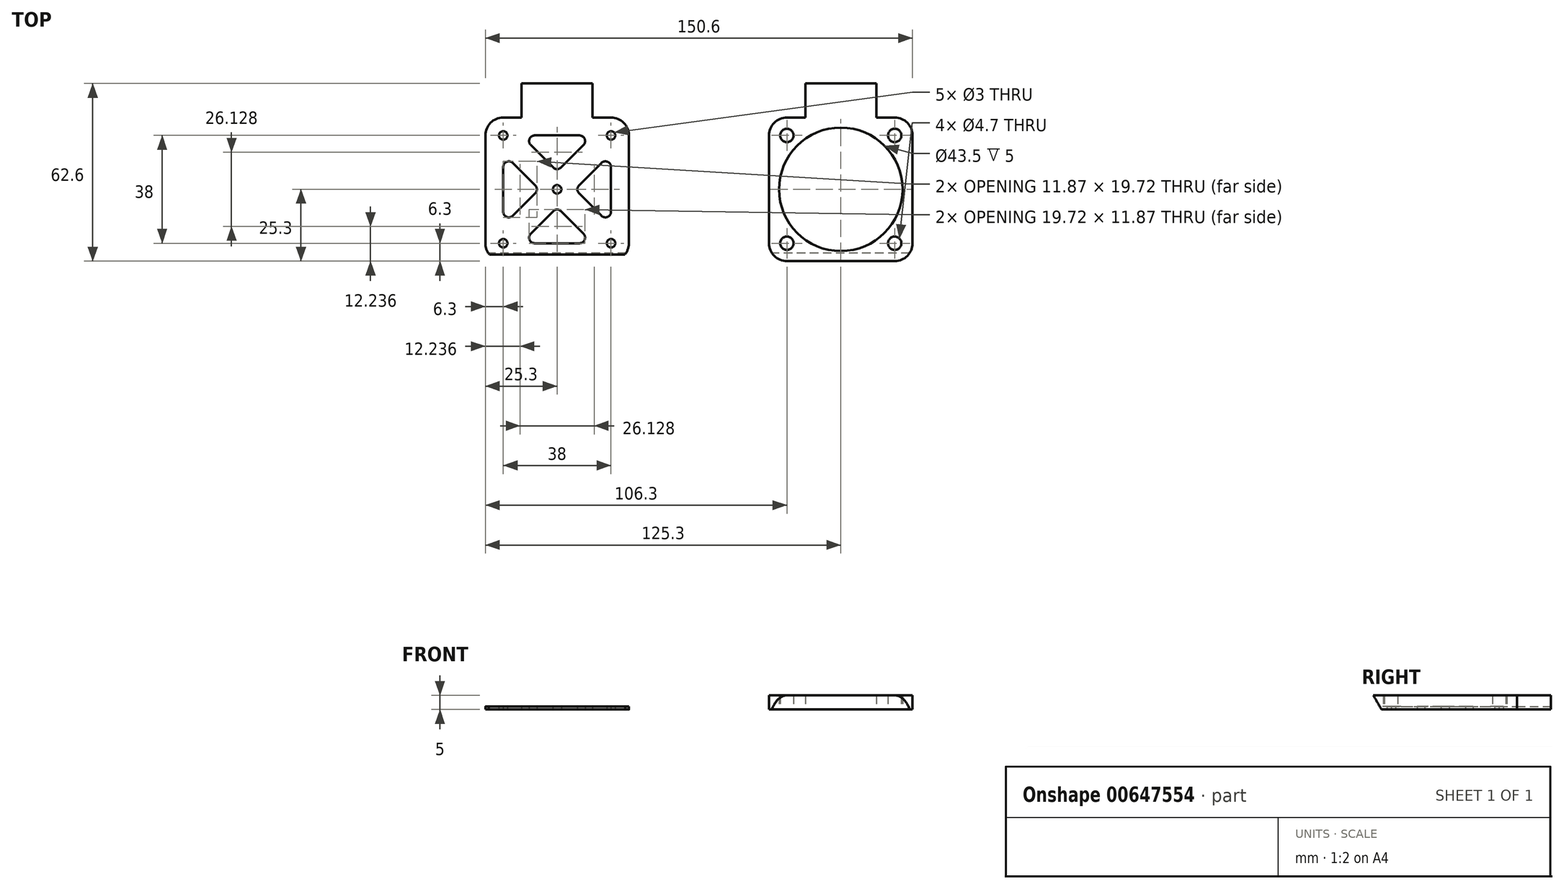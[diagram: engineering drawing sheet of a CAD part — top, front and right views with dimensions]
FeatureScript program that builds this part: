
annotation { "Feature Type Name" : "Feature", "Feature Type Description" : "" }
export const myFeature = defineFeature(function(context is Context, id is Id, definition is map)
    precondition{}
    {
        {
            var Q0;
            Q0=qCreatedBy(makeId("Top.planeOp"),FACE);
            var sketch = newSketch(context, id + "F0", { "sketchPlane" : qUnion([Q0])});
            skLineSegment(sketch, "E0.bottom", {"start": v(19, -25.3) * mm, "end": v(-19, -25.3) * mm});
            skLineSegment(sketch, "E0.top", {"start": v(19, 25.3) * mm, "end": v(-19, 25.3) * mm});
            skLineSegment(sketch, "E0.left", {"start": v(25.3, -19) * mm, "end": v(25.3, 19) * mm});
            skLineSegment(sketch, "E0.right", {"start": v(-25.3, -19) * mm, "end": v(-25.3, 19) * mm});
            skPoint(sketch, "E0.middle", {"position": v(0, 0) * mm});
            skLineSegment(sketch, "E1.bottom", {"start": v(-12.5, 25.3) * mm, "end": v(12.5, 25.3) * mm});
            skLineSegment(sketch, "E1.top", {"start": v(-12.5, 37.3) * mm, "end": v(12.5, 37.3) * mm});
            skLineSegment(sketch, "E1.left", {"start": v(-12.5, 25.3) * mm, "end": v(-12.5, 37.3) * mm});
            skLineSegment(sketch, "E1.right", {"start": v(12.5, 25.3) * mm, "end": v(12.5, 37.3) * mm});
            skPoint(sketch, "E2", {"position": v(0, 37.3) * mm});
            skCircle(sketch, "E3", {"center": v(0, 0) * mm, "radius": 21.75 * mm});
            skLineSegment(sketch, "E4.bottom", {"start": v(19, -19) * mm, "end": v(-19, -19) * mm, "construction": true});
            skLineSegment(sketch, "E4.top", {"start": v(19, 19) * mm, "end": v(-19, 19) * mm, "construction": true});
            skLineSegment(sketch, "E4.left", {"start": v(19, -19) * mm, "end": v(19, 19) * mm, "construction": true});
            skLineSegment(sketch, "E4.right", {"start": v(-19, -19) * mm, "end": v(-19, 19) * mm, "construction": true});
            skPoint(sketch, "E5.visualSharp", {"position": v(-25.3, 25.3) * mm});
            skArc(sketch, "E5.filletArc", {"start": v(-19, 25.3) * mm, "mid": v(-23.45, 23.45) * mm, "end": v(-25.3, 19) * mm});
            skPoint(sketch, "E6.visualSharp", {"position": v(25.3, 25.3) * mm});
            skArc(sketch, "E6.filletArc", {"start": v(25.3, 19) * mm, "mid": v(23.45, 23.45) * mm, "end": v(19, 25.3) * mm});
            skPoint(sketch, "E7.visualSharp", {"position": v(25.3, -25.3) * mm});
            skArc(sketch, "E7.filletArc", {"start": v(19, -25.3) * mm, "mid": v(23.45, -23.45) * mm, "end": v(25.3, -19) * mm});
            skPoint(sketch, "E8.visualSharp", {"position": v(-25.3, -25.3) * mm});
            skArc(sketch, "E8.filletArc", {"start": v(-25.3, -19) * mm, "mid": v(-23.45, -23.45) * mm, "end": v(-19, -25.3) * mm});
            skSolve(sketch);
        }
        {
            var Q0;
            Q0 = qSketchRegion(id + "F0", true);
            extrude(context, id + "F1", {"entities" : qUnion([Q0]), "depth" : 5 * mm, "offsetDistance" : 25 * mm});
        }
        {
            var Q0;
            Q0=sQuery(id+"F0.wireOp",VERTEX,"E4.bottom.end");
            var Q1;
            Q1=sQuery(id+"F0.wireOp",VERTEX,"E4.bottom.start");
            var Q2;
            Q2=sQuery(id+"F0.wireOp",VERTEX,"E4.top.end");
            var Q3;
            Q3=sQuery(id+"F0.wireOp",VERTEX,"E4.top.start");
            var Q4;
            Q4=makeQuery(id+"F1.opExtrude","SWEPT_BODY",BODY,{"disambiguationData":[OSD([sQuery(id+"F0.wireOp",EDGE,"E0.bottom"),sQuery(id+"F0.wireOp",EDGE,"E0.top"),sQuery(id+"F0.wireOp",EDGE,"E0.left"),sQuery(id+"F0.wireOp",EDGE,"E0.right"),sQuery(id+"F0.wireOp",EDGE,"E1.top"),sQuery(id+"F0.wireOp",EDGE,"E1.left"),sQuery(id+"F0.wireOp",EDGE,"E1.right"),sQuery(id+"F0.wireOp",EDGE,"E3"),sQuery(id+"F0.wireOp",EDGE,"E5.filletArc"),sQuery(id+"F0.wireOp",EDGE,"E6.filletArc"),sQuery(id+"F0.wireOp",EDGE,"E7.filletArc"),sQuery(id+"F0.wireOp",EDGE,"E8.filletArc")])]});
            hole(context, id + "F2", {"style" : HoleStyle.SIMPLE, "endStyle" : HoleEndStyle.THROUGH, "oppositeDirection" : true, "holeDiameter" : 4.7 * mm, "majorDiameter" : 5 * mm, "isTappedThrough" : true, "tappedDepth" : 12 * mm, "tapClearance" : 3, "startFromSketch" : true, "locations" : qUnion([Q0, Q1, Q2, Q3]), "scope" : qUnion([Q4])});
        }
        {
            var Q0;
            Q0=makeQuery(id+"F1.opExtrude","SWEPT_FACE",FACE,{"disambiguationData":[OSD([sQuery(id+"F0.wireOp",EDGE,"E0.right")])]});
            var sketch = newSketch(context, id + "F3", { "sketchPlane" : qUnion([Q0])});
            skLineSegment(sketch, "E9.0", {"start": v(19, 0) * mm, "end": v(25.3, 0) * mm});
            skLineSegment(sketch, "E10.0", {"start": v(25.3, 5) * mm, "end": v(25.3, 0) * mm});
            skLineSegment(sketch, "E11.0", {"start": v(19, 5) * mm, "end": v(25.3, 5) * mm, "construction": true});
            skLineSegment(sketch, "E12.0", {"start": v(19, 5) * mm, "end": v(19, 0) * mm, "construction": true});
            skLineSegment(sketch, "E13", {"start": v(22.41, 0) * mm, "end": v(25.3, 5) * mm});
            skPoint(sketch, "E14", {"position": v(25.3, 2.5) * mm});
            skLineSegment(sketch, "E15.0", {"start": v(-37.3, 5) * mm, "end": v(-37.3, 0) * mm, "construction": true});
            skSolve(sketch);
        }
        {
            var Q0;
            {var subQ0=sQuery(id+"F3.wireOp",EDGE,"E10.0");Q0=makeQuery(id+"F3.imprint","IMPRINT",FACE,{"disambiguationData":[TD([[makeQuery(id+"F3.imprint","IMPRINT",EDGE,{"derivedFrom":subQ0}),-1.0]])]});}
            var Q1;
            Q1=makeQuery(id+"F1.opExtrude","SWEPT_FACE",FACE,{"disambiguationData":[OSD([sQuery(id+"F0.wireOp",EDGE,"E0.left")])]});
            extrude(context, id + "F4", {"entities" : qUnion([Q0]), "operationType" : NewBodyOperationType.REMOVE, "endBound" : BoundingType.UP_TO_SURFACE, "oppositeDirection" : true, "depth" : 25 * mm, "endBoundEntityFace" : qUnion([Q1]), "offsetDistance" : 25 * mm});
        }
        {
            var Q0;
            Q0=qCreatedBy(makeId("Top.planeOp"),FACE);
            var sketch = newSketch(context, id + "F5", { "sketchPlane" : qUnion([Q0])});
            skLineSegment(sketch, "E16.0", {"start": v(-25.3, -19) * mm, "end": v(-25.3, 19) * mm});
            skPoint(sketch, "E17.0", {"position": v(-24.3, -22.41) * mm});
            skArc(sketch, "E18.0", {"start": v(-25.3, -19) * mm, "mid": v(-25.04, -20.78) * mm, "end": v(-24.3, -22.41) * mm});
            skLineSegment(sketch, "E19.0", {"start": v(24.3, -22.41) * mm, "end": v(-24.3, -22.41) * mm});
            skArc(sketch, "E20.0", {"start": v(24.3, -22.41) * mm, "mid": v(25.04, -20.78) * mm, "end": v(25.3, -19) * mm});
            skLineSegment(sketch, "E21.0", {"start": v(25.3, -19) * mm, "end": v(25.3, 19) * mm});
            skArc(sketch, "E22.0", {"start": v(25.3, 19) * mm, "mid": v(23.45, 23.45) * mm, "end": v(19, 25.3) * mm});
            skLineSegment(sketch, "E23.0", {"start": v(19, 25.3) * mm, "end": v(12.5, 25.3) * mm});
            skLineSegment(sketch, "E24.0", {"start": v(12.5, 25.3) * mm, "end": v(12.5, 37.3) * mm});
            skLineSegment(sketch, "E25.0", {"start": v(-12.5, 37.3) * mm, "end": v(12.5, 37.3) * mm});
            skLineSegment(sketch, "E26.0", {"start": v(-12.5, 25.3) * mm, "end": v(-12.5, 37.3) * mm});
            skLineSegment(sketch, "E27.0", {"start": v(-12.5, 25.3) * mm, "end": v(-19, 25.3) * mm});
            skArc(sketch, "E28.0", {"start": v(-19, 25.3) * mm, "mid": v(-23.45, 23.45) * mm, "end": v(-25.3, 19) * mm});
            skLineSegment(sketch, "E29.0.0", {"start": v(-25.3, 19) * mm, "end": v(-25.3, -19) * mm});
            skCircle(sketch, "E30", {"center": v(0, 0) * mm, "radius": 1.5 * mm});
            skCircle(sketch, "E31", {"center": v(-19, 19) * mm, "radius": 1.5 * mm});
            skCircle(sketch, "E32", {"center": v(-19, 19) * mm, "radius": 6.3 * mm});
            skCircle(sketch, "E33", {"center": v(19, 19) * mm, "radius": 1.5 * mm});
            skCircle(sketch, "E34", {"center": v(19, 19) * mm, "radius": 6.3 * mm});
            skArc(sketch, "E35", {"start": v(24.3, -22.41) * mm, "mid": v(19, -12.7) * mm, "end": v(13.7, -22.41) * mm});
            skArc(sketch, "E36", {"start": v(-13.7, -22.41) * mm, "mid": v(-19, -12.7) * mm, "end": v(-24.3, -22.41) * mm});
            skLineSegment(sketch, "E37", {"start": v(-19, 7.87) * mm, "end": v(-19, -7.87) * mm});
            skLineSegment(sketch, "E38", {"start": v(-7.87, -19) * mm, "end": v(7.87, -19) * mm});
            skLineSegment(sketch, "E39", {"start": v(19, -7.87) * mm, "end": v(19, 7.87) * mm});
            skLineSegment(sketch, "E40", {"start": v(7.87, 19) * mm, "end": v(-7.87, 19) * mm});
            skLineSegment(sketch, "E41", {"start": v(-9.29, 15.59) * mm, "end": v(-1.41, 7.71) * mm});
            skLineSegment(sketch, "E42", {"start": v(9.29, -15.59) * mm, "end": v(1.41, -7.71) * mm});
            skLineSegment(sketch, "E43", {"start": v(-15.59, -9.29) * mm, "end": v(-7.71, -1.41) * mm});
            skLineSegment(sketch, "E44", {"start": v(-9.29, -15.59) * mm, "end": v(-1.41, -7.71) * mm});
            skPoint(sketch, "E45.visualSharp", {"position": v(-19, 12.7) * mm});
            skArc(sketch, "E45.filletArc", {"start": v(-15.59, 9.29) * mm, "mid": v(-17.77, 9.72) * mm, "end": v(-19, 7.87) * mm});
            skPoint(sketch, "E46.visualSharp", {"position": v(-19, -12.7) * mm});
            skArc(sketch, "E46.filletArc", {"start": v(-19, -7.87) * mm, "mid": v(-17.77, -9.72) * mm, "end": v(-15.59, -9.29) * mm});
            skPoint(sketch, "E47.visualSharp", {"position": v(-12.7, -19) * mm});
            skArc(sketch, "E47.filletArc", {"start": v(-9.29, -15.59) * mm, "mid": v(-9.72, -17.77) * mm, "end": v(-7.87, -19) * mm});
            skPoint(sketch, "E48.visualSharp", {"position": v(12.7, -19) * mm});
            skArc(sketch, "E48.filletArc", {"start": v(7.87, -19) * mm, "mid": v(9.72, -17.77) * mm, "end": v(9.29, -15.59) * mm});
            skPoint(sketch, "E49.visualSharp", {"position": v(19, -12.7) * mm});
            skArc(sketch, "E49.filletArc", {"start": v(15.59, -9.29) * mm, "mid": v(17.77, -9.72) * mm, "end": v(19, -7.87) * mm});
            skPoint(sketch, "E50.visualSharp", {"position": v(-12.7, 19) * mm});
            skArc(sketch, "E50.filletArc", {"start": v(-7.87, 19) * mm, "mid": v(-9.72, 17.77) * mm, "end": v(-9.29, 15.59) * mm});
            skPoint(sketch, "E51.visualSharp", {"position": v(12.7, 19) * mm});
            skArc(sketch, "E51.filletArc", {"start": v(9.29, 15.59) * mm, "mid": v(9.72, 17.77) * mm, "end": v(7.87, 19) * mm});
            skPoint(sketch, "E52.visualSharp", {"position": v(19, 12.7) * mm});
            skArc(sketch, "E52.filletArc", {"start": v(19, 7.87) * mm, "mid": v(17.77, 9.72) * mm, "end": v(15.59, 9.29) * mm});
            skLineSegment(sketch, "E53.trimOffspring", {"start": v(1.41, 7.71) * mm, "end": v(9.29, 15.59) * mm});
            skLineSegment(sketch, "E54.trimOffspring", {"start": v(7.71, 1.41) * mm, "end": v(15.59, 9.29) * mm});
            skLineSegment(sketch, "E55.trimOffspring", {"start": v(-7.71, 1.41) * mm, "end": v(-15.59, 9.29) * mm});
            skLineSegment(sketch, "E56.trimOffspring", {"start": v(7.71, -1.41) * mm, "end": v(15.59, -9.29) * mm});
            skPoint(sketch, "E57.visualSharp", {"position": v(-6.3, 0) * mm});
            skArc(sketch, "E57.filletArc", {"start": v(-7.71, -1.41) * mm, "mid": v(-7.13, 0) * mm, "end": v(-7.71, 1.41) * mm});
            skPoint(sketch, "E58.visualSharp", {"position": v(0, 6.3) * mm});
            skArc(sketch, "E58.filletArc", {"start": v(-1.41, 7.71) * mm, "mid": v(0, 7.13) * mm, "end": v(1.41, 7.71) * mm});
            skPoint(sketch, "E59.visualSharp", {"position": v(6.3, 0) * mm});
            skArc(sketch, "E59.filletArc", {"start": v(7.71, 1.41) * mm, "mid": v(7.13, 0) * mm, "end": v(7.71, -1.41) * mm});
            skPoint(sketch, "E60.visualSharp", {"position": v(0, -6.3) * mm});
            skArc(sketch, "E60.filletArc", {"start": v(1.41, -7.71) * mm, "mid": v(0, -7.13) * mm, "end": v(-1.41, -7.71) * mm});
            skCircle(sketch, "E61", {"center": v(-19, -19) * mm, "radius": 1.5 * mm});
            skCircle(sketch, "E62", {"center": v(19, -19) * mm, "radius": 1.5 * mm});
            skSolve(sketch);
        }
        {
            var Q0;
            Q0=makeQuery(id+"F1.opExtrude","SWEPT_BODY",BODY,{"disambiguationData":[OSD([sQuery(id+"F0.wireOp",EDGE,"E0.bottom"),sQuery(id+"F0.wireOp",EDGE,"E0.top"),sQuery(id+"F0.wireOp",EDGE,"E0.left"),sQuery(id+"F0.wireOp",EDGE,"E0.right"),sQuery(id+"F0.wireOp",EDGE,"E1.top"),sQuery(id+"F0.wireOp",EDGE,"E1.left"),sQuery(id+"F0.wireOp",EDGE,"E1.right"),sQuery(id+"F0.wireOp",EDGE,"E3"),sQuery(id+"F0.wireOp",EDGE,"E5.filletArc"),sQuery(id+"F0.wireOp",EDGE,"E6.filletArc"),sQuery(id+"F0.wireOp",EDGE,"E7.filletArc"),sQuery(id+"F0.wireOp",EDGE,"E8.filletArc")])]});
            transform(context, id + "F6", {"entities" : qUnion([Q0]), "transformType" : TransformType.TRANSLATION_3D, "dx" : 100 * mm, "dy" : 0 * mm, "dz" : 0 * mm, "makeCopy" : false});
        }
        {
            var Q0;
            {var subQ5=sQuery(id+"F5.wireOp",EDGE,"E21.0");Q0=makeQuery(id+"F5.imprint","IMPRINT",FACE,{"disambiguationData":[TD([[makeQuery(id+"F5.imprint","IMPRINT",EDGE,{"derivedFrom":subQ5}),1.0]])]});}
            var Q1;
            Q1=makeQuery(id+"F5.imprint","IMPRINT",FACE,{"disambiguationData":[TD([[makeQuery(id+"F5.imprint","IMPRINT",EDGE,{"derivedFrom":sQuery(id+"F5.wireOp",EDGE,"E33")}),-1.0]])]});
            var Q2;
            Q2=makeQuery(id+"F5.imprint","IMPRINT",FACE,{"disambiguationData":[TD([[makeQuery(id+"F5.imprint","IMPRINT",EDGE,{"derivedFrom":sQuery(id+"F5.wireOp",EDGE,"E62")}),-1.0]])]});
            var Q3;
            Q3=makeQuery(id+"F5.imprint","IMPRINT",FACE,{"disambiguationData":[TD([[makeQuery(id+"F5.imprint","IMPRINT",EDGE,{"derivedFrom":sQuery(id+"F5.wireOp",EDGE,"E61")}),-1.0]])]});
            var Q4;
            Q4=makeQuery(id+"F5.imprint","IMPRINT",FACE,{"disambiguationData":[TD([[makeQuery(id+"F5.imprint","IMPRINT",EDGE,{"derivedFrom":sQuery(id+"F5.wireOp",EDGE,"E31")}),-1.0]])]});
            extrude(context, id + "F7", {"entities" : qUnion([Q0, Q1, Q2, Q3, Q4]), "depth" : 1 * mm, "offsetDistance" : 25 * mm});
        }
        {
            var Q0;
            Q0=makeQuery(id+"F7.opExtrude","SWEPT_FACE",FACE,{"disambiguationData":[OSD([sQuery(id+"F5.wireOp",EDGE,"E16.0")])]});
            var sketch = newSketch(context, id + "F8", { "sketchPlane" : qUnion([Q0])});
            skLineSegment(sketch, "E63.0", {"start": v(19, 0) * mm, "end": v(22.41, 0) * mm});
            skLineSegment(sketch, "E64.0", {"start": v(22.41, 1) * mm, "end": v(22.41, 0) * mm});
            skLineSegment(sketch, "E65.0", {"start": v(25.3, 5) * mm, "end": v(22.41, 0) * mm});
            skLineSegment(sketch, "E66", {"start": v(22.41, 1) * mm, "end": v(23, 1) * mm});
            skSolve(sketch);
        }
        {
            var Q0;
            {var subQ0=sQuery(id+"F8.wireOp",EDGE,"E64.0");Q0=makeQuery(id+"F8.imprint","IMPRINT",FACE,{"disambiguationData":[TD([[makeQuery(id+"F8.imprint","IMPRINT",EDGE,{"derivedFrom":subQ0}),1.0]])]});}
            var Q1;
            Q1=makeQuery(id+"F7.opExtrude","SWEPT_FACE",FACE,{"disambiguationData":[OSD([sQuery(id+"F5.wireOp",EDGE,"E21.0")])]});
            extrude(context, id + "F9", {"entities" : qUnion([Q0]), "operationType" : NewBodyOperationType.ADD, "endBound" : BoundingType.UP_TO_SURFACE, "oppositeDirection" : true, "depth" : 25 * mm, "endBoundEntityFace" : qUnion([Q1]), "offsetDistance" : 25 * mm});
        }
        {
            var Q0;
            Q0=makeQuery(id+"F9.boolean.opBoolean","MERGE",FACE,{"derivedFrom":[makeQuery(id+"F7.opExtrude","CAP_FACE",FACE,{"disambiguationData":[OSD([sQuery(id+"F5.wireOp",EDGE,"E19.0"),sQuery(id+"F5.wireOp",EDGE,"E21.0"),sQuery(id+"F5.wireOp",EDGE,"E23.0"),sQuery(id+"F5.wireOp",EDGE,"E24.0"),sQuery(id+"F5.wireOp",EDGE,"E25.0"),sQuery(id+"F5.wireOp",EDGE,"E26.0"),sQuery(id+"F5.wireOp",EDGE,"E27.0"),sQuery(id+"F5.wireOp",EDGE,"E16.0"),sQuery(id+"F5.wireOp",EDGE,"E30"),sQuery(id+"F5.wireOp",EDGE,"E31"),sQuery(id+"F5.wireOp",EDGE,"E32"),sQuery(id+"F5.wireOp",EDGE,"E33"),sQuery(id+"F5.wireOp",EDGE,"E34"),sQuery(id+"F5.wireOp",EDGE,"E35"),sQuery(id+"F5.wireOp",EDGE,"E36"),sQuery(id+"F5.wireOp",EDGE,"E37"),sQuery(id+"F5.wireOp",EDGE,"E38"),sQuery(id+"F5.wireOp",EDGE,"E39"),sQuery(id+"F5.wireOp",EDGE,"E40"),sQuery(id+"F5.wireOp",EDGE,"E41"),sQuery(id+"F5.wireOp",EDGE,"E42"),sQuery(id+"F5.wireOp",EDGE,"E43"),sQuery(id+"F5.wireOp",EDGE,"E44"),sQuery(id+"F5.wireOp",EDGE,"E45.filletArc"),sQuery(id+"F5.wireOp",EDGE,"E46.filletArc"),sQuery(id+"F5.wireOp",EDGE,"E47.filletArc"),sQuery(id+"F5.wireOp",EDGE,"E48.filletArc"),sQuery(id+"F5.wireOp",EDGE,"E49.filletArc"),sQuery(id+"F5.wireOp",EDGE,"E50.filletArc"),sQuery(id+"F5.wireOp",EDGE,"E51.filletArc"),sQuery(id+"F5.wireOp",EDGE,"E52.filletArc"),sQuery(id+"F5.wireOp",EDGE,"E53.trimOffspring"),sQuery(id+"F5.wireOp",EDGE,"E54.trimOffspring"),sQuery(id+"F5.wireOp",EDGE,"E55.trimOffspring"),sQuery(id+"F5.wireOp",EDGE,"E56.trimOffspring"),sQuery(id+"F5.wireOp",EDGE,"E57.filletArc"),sQuery(id+"F5.wireOp",EDGE,"E58.filletArc"),sQuery(id+"F5.wireOp",EDGE,"E59.filletArc"),sQuery(id+"F5.wireOp",EDGE,"E60.filletArc"),sQuery(id+"F5.wireOp",EDGE,"E61"),sQuery(id+"F5.wireOp",EDGE,"E62")])],"isStart":false}),makeQuery(id+"F9.opExtrude","SWEPT_FACE",FACE,{"disambiguationData":[OSD([sQuery(id+"F8.wireOp",EDGE,"E66")])]})]});
            var sketch = newSketch(context, id + "F10", { "sketchPlane" : qUnion([Q0])});
            skArc(sketch, "E67.0", {"start": v(-25.3, -19) * mm, "mid": v(-24.93, -21.12) * mm, "end": v(-23.87, -23) * mm});
            skArc(sketch, "E68.0", {"start": v(23.87, -23) * mm, "mid": v(24.93, -21.12) * mm, "end": v(25.3, -19) * mm});
            skLineSegment(sketch, "E69.0", {"start": v(25.3, -23) * mm, "end": v(-25.3, -23) * mm});
            skPoint(sketch, "E70.orphan", {"position": v(24.3, -22.41) * mm});
            skPoint(sketch, "E71.orphan", {"position": v(-24.3, -22.41) * mm});
            skSolve(sketch);
        }
        {
            var Q0;
            {var subQ1=sQuery(id+"F8.wireOp",EDGE,"E66");var subQ7=makeQuery(id+"F9.opExtrude","CAP_EDGE",EDGE,{"disambiguationData":[OSD([subQ1])],"isStart":true});Q0=makeQuery(id+"F10.imprint","IMPRINT",FACE,{"disambiguationData":[TD([[makeQuery(id+"F10.imprint","IMPRINT",EDGE,{"derivedFrom":subQ7}),1.0]])]});}
            var Q1;
            {var subQ2=sQuery(id+"F8.wireOp",EDGE,"E66");var subQ7=makeQuery(id+"F9.opExtrude","CAP_EDGE",EDGE,{"disambiguationData":[OSD([subQ2])],"isStart":false});Q1=makeQuery(id+"F10.imprint","IMPRINT",FACE,{"disambiguationData":[TD([[makeQuery(id+"F10.imprint","IMPRINT",EDGE,{"derivedFrom":subQ7}),1.0]])]});}
            extrude(context, id + "F11", {"entities" : qUnion([Q0, Q1]), "operationType" : NewBodyOperationType.REMOVE, "oppositeDirection" : true, "depth" : 25 * mm, "offsetDistance" : 25 * mm});
        }
    });
